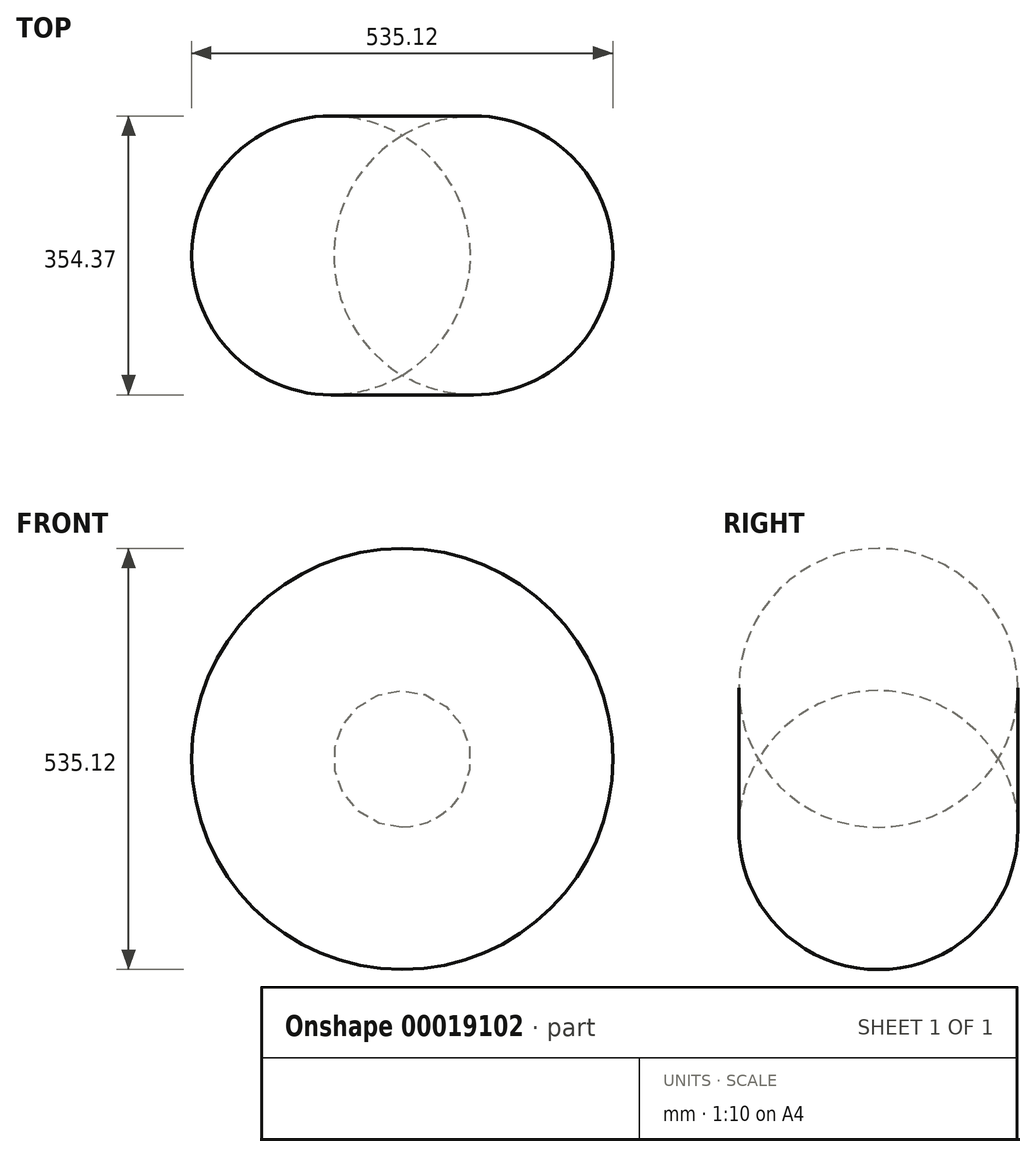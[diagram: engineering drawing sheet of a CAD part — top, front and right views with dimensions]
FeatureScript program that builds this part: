
annotation { "Feature Type Name" : "Feature", "Feature Type Description" : "" }
export const myFeature = defineFeature(function(context is Context, id is Id, definition is map)
    precondition{}
    {
        {
            var Q0;
            Q0=qCreatedBy(makeId("Top.planeOp"),FACE);
            var sketch = newSketch(context, id + "F0", { "sketchPlane" : qUnion([Q0])});
            skLineSegment(sketch, "E0", {"start": v(0, 151.99) * mm, "end": v(0, -152.81) * mm});
            skArc(sketch, "E1", {"start": v(0, -152.81) * mm, "mid": v(86.8, -0.41) * mm, "end": v(0, 151.99) * mm});
            skSolve(sketch);
        }
        {
            var Q0;
            Q0=makeQuery(id+"F0.imprint","IMPRINT",FACE,{"disambiguationData":[TD([[makeQuery(id+"F0.imprint","IMPRINT",EDGE,{"derivedFrom":sQuery(id+"F0.wireOp",EDGE,"E0")}),1.0]])]});
            var Q1;
            Q1=sQuery(id+"F0.wireOp",EDGE,"E0");
            revolve(context, id + "F1", {"entities" : qUnion([Q0]), "axis" : qUnion([Q1]), "revolveType" : RevolveType.FULL});
        }
    });
